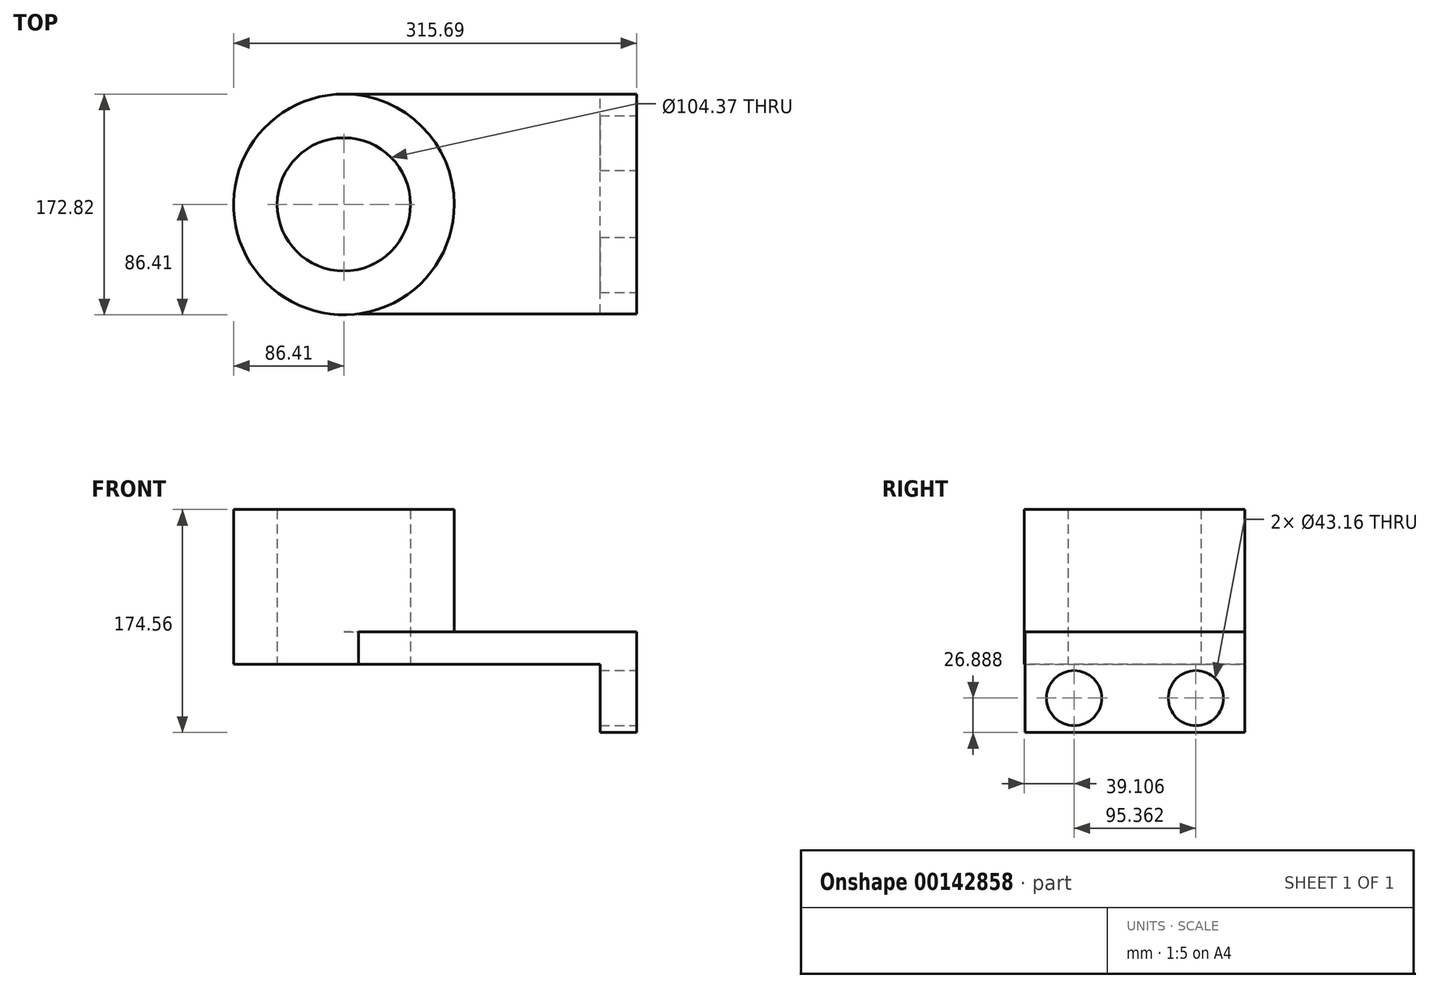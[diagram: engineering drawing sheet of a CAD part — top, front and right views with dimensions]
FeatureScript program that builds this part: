
annotation { "Feature Type Name" : "Feature", "Feature Type Description" : "" }
export const myFeature = defineFeature(function(context is Context, id is Id, definition is map)
    precondition{}
    {
        {
            var Q0;
            Q0=qCreatedBy(makeId("Top.planeOp"),FACE);
            var sketch = newSketch(context, id + "F0", { "sketchPlane" : qUnion([Q0])});
            skCircle(sketch, "E0", {"center": v(0, 0) * mm, "radius": 86.4 * mm});
            skCircle(sketch, "E1", {"center": v(0, 0) * mm, "radius": 52.18 * mm});
            skLineSegment(sketch, "E2.bottom", {"start": v(0.08, 86.4) * mm, "end": v(229.28, 86.4) * mm});
            skLineSegment(sketch, "E2.top", {"start": v(0.08, -85.66) * mm, "end": v(229.28, -85.66) * mm});
            skLineSegment(sketch, "E2.left", {"start": v(0.08, 86.4) * mm, "end": v(0.08, -85.66) * mm});
            skLineSegment(sketch, "E2.right", {"start": v(229.28, 86.4) * mm, "end": v(229.28, -85.66) * mm});
            skSolve(sketch);
        }
        {
            var Q0;
            {var subQ0=sQuery(id+"F0.wireOp",EDGE,"E2.bottom");Q0=makeQuery(id+"F0.imprint","IMPRINT",FACE,{"disambiguationData":[TD([[makeQuery(id+"F0.imprint","IMPRINT",EDGE,{"derivedFrom":subQ0}),-1.0]])]});}
            var Q1;
            {var subQ0=sQuery(id+"F0.wireOp",EDGE,"E2.left");var subQ3=sQuery(id+"F0.wireOp",EDGE,"E1");var subQ4=makeQuery(id+"F0.imprint","INTERSECT",VERTEX,{"disambiguationData":[OD(0.0)],"derivedFrom":[subQ3,subQ0]});Q1=makeQuery(id+"F0.imprint","IMPRINT",FACE,{"disambiguationData":[TD([[makeQuery(id+"F0.imprint","IMPRINT",EDGE,{"disambiguationData":[TD([[subQ4,1.0]])],"derivedFrom":subQ3}),-1.0]])]});}
            var Q2;
            {var subQ0=sQuery(id+"F0.wireOp",EDGE,"E2.left");var subQ3=sQuery(id+"F0.wireOp",EDGE,"E1");var subQ4=makeQuery(id+"F0.imprint","INTERSECT",VERTEX,{"disambiguationData":[OD(0.0)],"derivedFrom":[subQ3,subQ0]});Q2=makeQuery(id+"F0.imprint","IMPRINT",FACE,{"disambiguationData":[TD([[makeQuery(id+"F0.imprint","IMPRINT",EDGE,{"disambiguationData":[TD([[subQ4,-1.0]])],"derivedFrom":subQ3}),-1.0]])]});}
            extrude(context, id + "F1", {"entities" : qUnion([Q0, Q1, Q2]), "depth" : 25.4 * mm});
        }
        {
            var Q0;
            {var subQ0=sQuery(id+"F0.wireOp",EDGE,"E2.left");var subQ3=sQuery(id+"F0.wireOp",EDGE,"E1");var subQ4=makeQuery(id+"F0.imprint","INTERSECT",VERTEX,{"disambiguationData":[OD(0.0)],"derivedFrom":[subQ3,subQ0]});Q0=makeQuery(id+"F0.imprint","IMPRINT",FACE,{"disambiguationData":[TD([[makeQuery(id+"F0.imprint","IMPRINT",EDGE,{"disambiguationData":[TD([[subQ4,-1.0]])],"derivedFrom":subQ3}),-1.0]])]});}
            var Q1;
            {var subQ0=sQuery(id+"F0.wireOp",EDGE,"E2.left");var subQ3=sQuery(id+"F0.wireOp",EDGE,"E1");var subQ4=makeQuery(id+"F0.imprint","INTERSECT",VERTEX,{"disambiguationData":[OD(0.0)],"derivedFrom":[subQ3,subQ0]});Q1=makeQuery(id+"F0.imprint","IMPRINT",FACE,{"disambiguationData":[TD([[makeQuery(id+"F0.imprint","IMPRINT",EDGE,{"disambiguationData":[TD([[subQ4,1.0]])],"derivedFrom":subQ3}),-1.0]])]});}
            var Q2;
            Q2=sQuery(id+"F0.wireOp",EDGE,"E0");
            extrude(context, id + "F4", {"entities" : qUnion([Q0, Q1]), "operationType" : NewBodyOperationType.ADD, "surfaceEntities" : qUnion([Q2]), "depth" : 121.3 * mm});
        }
        {
            var Q0;
            Q0=makeQuery(id+"F1.opExtrude","SWEPT_FACE",FACE,{"disambiguationData":[OSD([sQuery(id+"F0.wireOp",EDGE,"E2.right")])]});
            var sketch = newSketch(context, id + "F5", { "sketchPlane" : qUnion([Q0])});
            skLineSegment(sketch, "E3.bottom", {"start": v(-85.66, 25.4) * mm, "end": v(86.4, 25.4) * mm});
            skLineSegment(sketch, "E3.top", {"start": v(-85.66, -53.26) * mm, "end": v(86.4, -53.26) * mm});
            skLineSegment(sketch, "E3.left", {"start": v(-85.66, 25.4) * mm, "end": v(-85.66, -53.26) * mm});
            skLineSegment(sketch, "E3.right", {"start": v(86.4, 25.4) * mm, "end": v(86.4, -53.26) * mm});
            skSolve(sketch);
        }
        {
            var Q0;
            {var subQ0=sQuery(id+"F5.wireOp",EDGE,"E3.top");Q0=makeQuery(id+"F5.imprint","IMPRINT",FACE,{"disambiguationData":[TD([[makeQuery(id+"F5.imprint","IMPRINT",EDGE,{"derivedFrom":subQ0}),1.0]])]});}
            var Q1;
            {var subQ0=sQuery(id+"F5.wireOp",EDGE,"E3.bottom");Q1=makeQuery(id+"F5.imprint","IMPRINT",FACE,{"disambiguationData":[TD([[makeQuery(id+"F5.imprint","IMPRINT",EDGE,{"derivedFrom":subQ0}),1.0]])]});}
            var Q2;
            Q2=sQuery(id+"F5.wireOp",EDGE,"E3.left");
            var Q3;
            Q3=sQuery(id+"F5.wireOp",EDGE,"E3.top");
            var Q4;
            Q4=sQuery(id+"F5.wireOp",EDGE,"E3.bottom");
            var Q5;
            Q5=sQuery(id+"F5.wireOp",EDGE,"E3.right");
            extrude(context, id + "F2", {"entities" : qUnion([Q0, Q1]), "operationType" : NewBodyOperationType.ADD, "surfaceEntities" : qUnion([Q2, Q3, Q4, Q5]), "oppositeDirection" : true, "depth" : 28.62 * mm});
        }
        {
            var Q0;
            Q0=makeQuery(id+"F2.boolean.opBoolean","MERGE",FACE,{"derivedFrom":[makeQuery(id+"F1.opExtrude","SWEPT_FACE",FACE,{"disambiguationData":[OSD([sQuery(id+"F0.wireOp",EDGE,"E2.right")])]}),makeQuery(id+"F2.opExtrude","CAP_FACE",FACE,{"disambiguationData":[OSD([sQuery(id+"F5.wireOp",EDGE,"E3.bottom"),sQuery(id+"F5.wireOp",EDGE,"E3.top"),sQuery(id+"F5.wireOp",EDGE,"E3.left"),sQuery(id+"F5.wireOp",EDGE,"E3.right")])],"isStart":true})]});
            var sketch = newSketch(context, id + "F6", { "sketchPlane" : qUnion([Q0])});
            skLineSegment(sketch, "E4", {"start": v(0.38, -53.26) * mm, "end": v(0.38, 25.4) * mm, "construction": true});
            skCircle(sketch, "E5", {"center": v(-47.3, -26.37) * mm, "radius": 21.58 * mm});
            skCircle(sketch, "E6.MirrorC", {"center": v(48.06, -26.37) * mm, "radius": 21.58 * mm});
            skSolve(sketch);
        }
        {
            var Q0;
            Q0 = qSketchRegion(id + "F6", true);
            var Q1;
            Q1=sQuery(id+"F6.wireOp",EDGE,"E6.MirrorC");
            var Q2;
            Q2=sQuery(id+"F6.wireOp",EDGE,"E5");
            extrude(context, id + "F3", {"entities" : qUnion([Q0]), "operationType" : NewBodyOperationType.REMOVE, "surfaceEntities" : qUnion([Q1, Q2]), "endBound" : BoundingType.UP_TO_NEXT, "oppositeDirection" : true, "depth" : 25.4 * mm});
        }
    });
